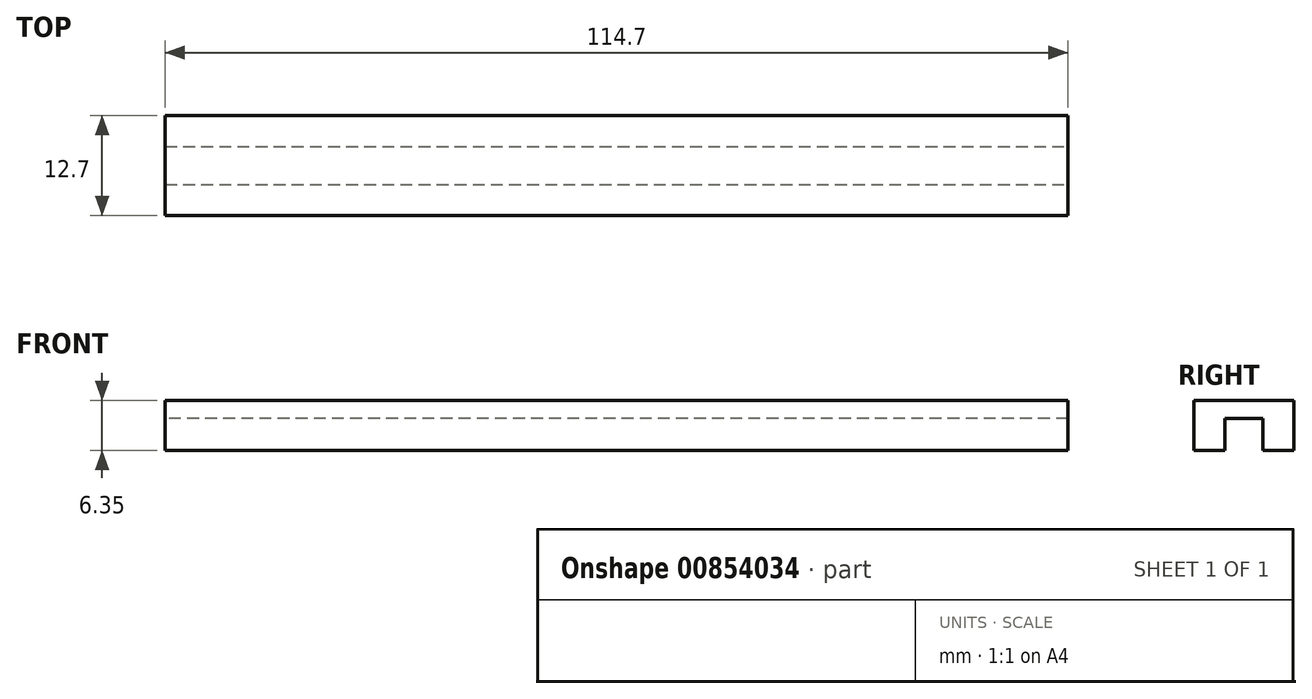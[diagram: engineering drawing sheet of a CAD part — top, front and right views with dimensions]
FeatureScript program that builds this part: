
annotation { "Feature Type Name" : "Feature", "Feature Type Description" : "" }
export const myFeature = defineFeature(function(context is Context, id is Id, definition is map)
    precondition{}
    {
        {
            var Q0;
            Q0=qCreatedBy(makeId("Top.planeOp"),FACE);
            var sketch = newSketch(context, id + "F0", { "sketchPlane" : qUnion([Q0])});
            skLineSegment(sketch, "E0.bottom", {"start": v(0, 0) * mm, "end": v(114.7, 0) * mm});
            skLineSegment(sketch, "E0.top", {"start": v(0, 12.7) * mm, "end": v(114.7, 12.7) * mm});
            skLineSegment(sketch, "E0.left", {"start": v(0, 0) * mm, "end": v(0, 12.7) * mm});
            skLineSegment(sketch, "E0.right", {"start": v(114.7, 0) * mm, "end": v(114.7, 12.7) * mm});
            skSolve(sketch);
        }
        {
            var Q0;
            Q0=makeQuery(id+"F0.imprint","IMPRINT",FACE,{"disambiguationData":[TD([[makeQuery(id+"F0.imprint","IMPRINT",EDGE,{"derivedFrom":sQuery(id+"F0.wireOp",EDGE,"E0.bottom")}),1.0]])]});
            extrude(context, id + "F1", {"entities" : qUnion([Q0]), "depth" : 6.35 * mm, "offsetDistance" : 25.4 * mm});
        }
        {
            var Q0;
            Q0=makeQuery(id+"F1.opExtrude","SWEPT_FACE",FACE,{"disambiguationData":[OSD([sQuery(id+"F0.wireOp",EDGE,"E0.left")])]});
            var sketch = newSketch(context, id + "F2", { "sketchPlane" : qUnion([Q0])});
            skLineSegment(sketch, "E1.bottom", {"start": v(-3.91, -4.03) * mm, "end": v(-8.78, -4.03) * mm});
            skLineSegment(sketch, "E1.top", {"start": v(-3.91, 4.03) * mm, "end": v(-8.78, 4.03) * mm});
            skLineSegment(sketch, "E1.left", {"start": v(-3.91, -4.03) * mm, "end": v(-3.91, 4.03) * mm});
            skLineSegment(sketch, "E1.right", {"start": v(-8.78, -4.03) * mm, "end": v(-8.78, 4.03) * mm});
            skPoint(sketch, "E1.middle", {"position": v(-6.35, 0) * mm});
            skSolve(sketch);
        }
        {
            var Q0;
            Q0 = qSketchRegion(id + "F2", true);
            extrude(context, id + "F3", {"entities" : qUnion([Q0]), "operationType" : NewBodyOperationType.REMOVE, "endBound" : BoundingType.THROUGH_ALL, "oppositeDirection" : true, "depth" : 25.4 * mm, "offsetDistance" : 25.4 * mm});
        }
    });
